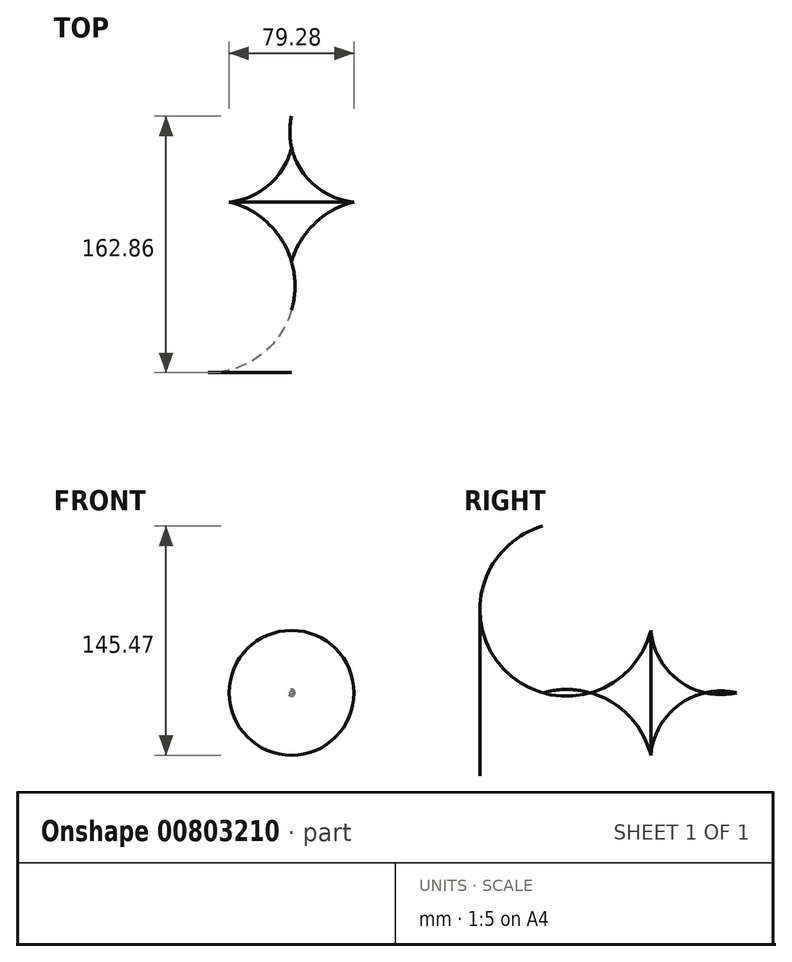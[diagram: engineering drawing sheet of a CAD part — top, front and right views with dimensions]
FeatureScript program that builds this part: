
annotation { "Feature Type Name" : "Feature", "Feature Type Description" : "" }
export const myFeature = defineFeature(function(context is Context, id is Id, definition is map)
    precondition{}
    {
        {
            var Q0;
            Q0=qCreatedBy(makeId("Top.planeOp"),FACE);
            var sketch = newSketch(context, id + "F0", { "sketchPlane" : qUnion([Q0])});
            skLineSegment(sketch, "E0", {"start": v(0, 75.7) * mm, "end": v(0, -74.65) * mm, "construction": true});
            skArc(sketch, "E1", {"start": v(39.64, 0) * mm, "mid": v(14.72, -13.77) * mm, "end": v(0, -38.16) * mm});
            skArc(sketch, "E2", {"start": v(0, 34.64) * mm, "mid": v(14.17, 10.86) * mm, "end": v(39.64, 0) * mm});
            skLineSegment(sketch, "E3", {"start": v(0, 34.64) * mm, "end": v(0, -38.16) * mm});
            skSolve(sketch);
        }
        {
            var Q0;
            Q0=makeQuery(id+"F0.imprint","IMPRINT",FACE,{"disambiguationData":[TD([[makeQuery(id+"F0.imprint","IMPRINT",EDGE,{"derivedFrom":sQuery(id+"F0.wireOp",EDGE,"E1")}),-1.0]])]});
            var Q1;
            Q1=sQuery(id+"F0.wireOp",EDGE,"E0");
            revolve(context, id + "F1", {"surfaceOperationType" : NewSurfaceOperationType.NEW, "entities" : qUnion([Q0]), "axis" : qUnion([Q1]), "revolveType" : RevolveType.FULL});
        }
    });
